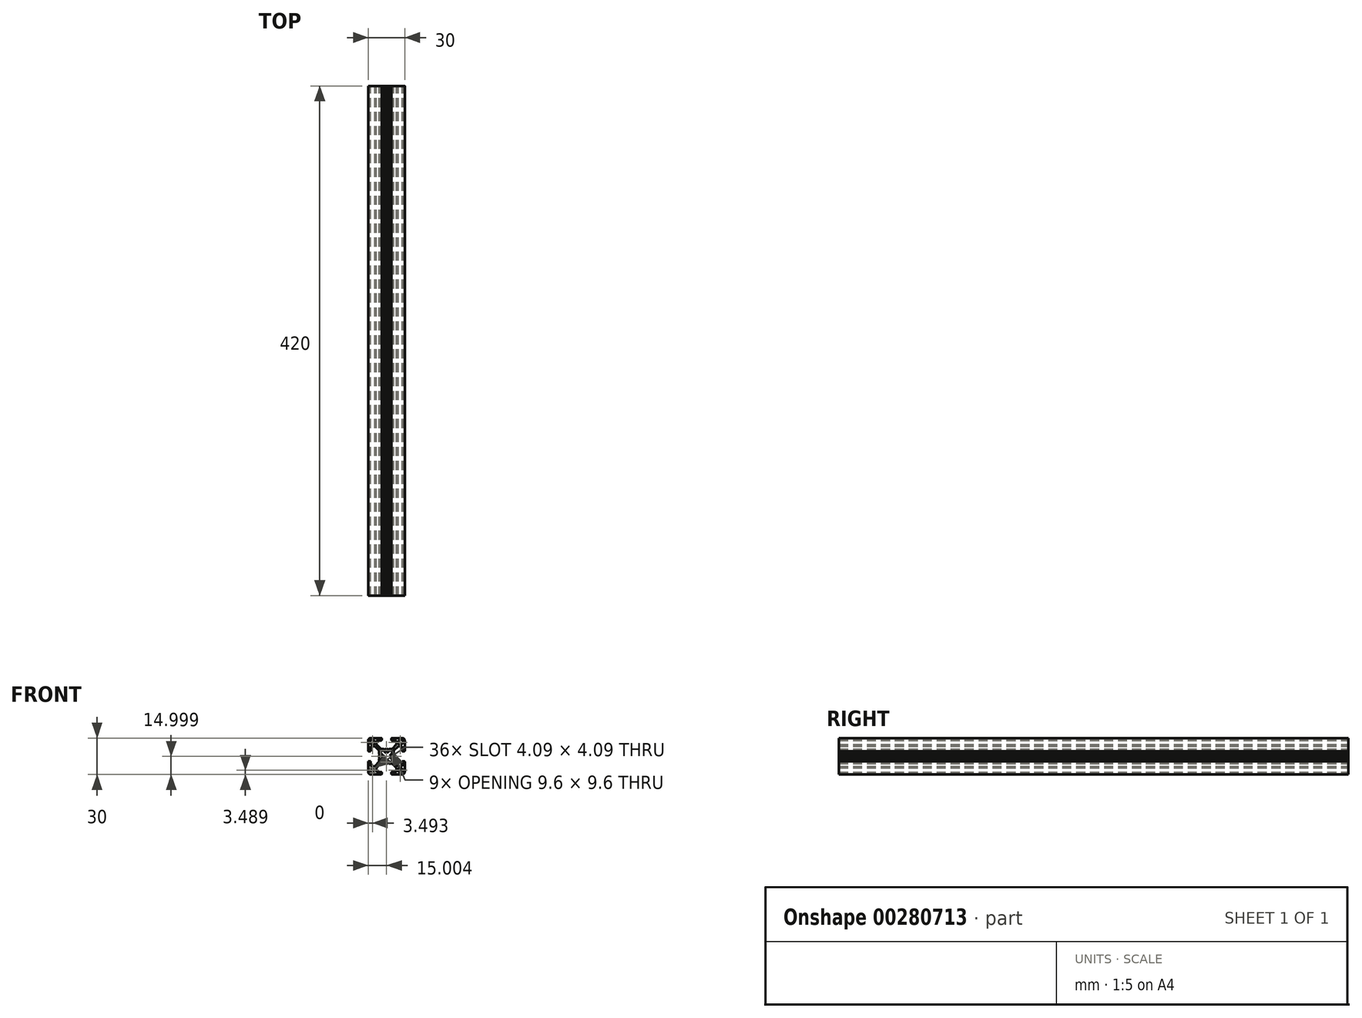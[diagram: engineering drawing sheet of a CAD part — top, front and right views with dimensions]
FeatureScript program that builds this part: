
annotation { "Feature Type Name" : "Feature", "Feature Type Description" : "" }
export const myFeature = defineFeature(function(context is Context, id is Id, definition is map)
    precondition{}
    {
        {
            var Q0;
            Q0=qCreatedBy(makeId("Front.planeOp"),FACE);
            var sketch = newSketch(context, id + "F0", { "sketchPlane" : qUnion([Q0])});
            skArc(sketch, "E0", {"start": v(22.08, 23.36) * mm, "mid": v(21.8, 23.24) * mm, "end": v(21.68, 22.96) * mm});
            skArc(sketch, "E1", {"start": v(21.68, 14.16) * mm, "mid": v(21.8, 13.88) * mm, "end": v(22.08, 13.76) * mm});
            skArc(sketch, "E2", {"start": v(11.48, 5.56) * mm, "mid": v(12.07, 4.15) * mm, "end": v(13.48, 3.56) * mm});
            skLineSegment(sketch, "E3", {"start": v(11.48, 14.16) * mm, "end": v(11.48, 5.56) * mm});
            skLineSegment(sketch, "E4", {"start": v(18.23, 5.56) * mm, "end": v(18.23, 8.9) * mm});
            skLineSegment(sketch, "E5", {"start": v(22.08, 3.56) * mm, "end": v(13.48, 3.56) * mm});
            skLineSegment(sketch, "E6", {"start": v(22.08, 5.56) * mm, "end": v(18.23, 5.56) * mm});
            skLineSegment(sketch, "E7", {"start": v(22.48, 5.16) * mm, "end": v(22.48, 3.96) * mm});
            skLineSegment(sketch, "E8", {"start": v(13.48, 10.3) * mm, "end": v(16.82, 10.3) * mm});
            skLineSegment(sketch, "E9", {"start": v(20.48, 13.97) * mm, "end": v(16.82, 10.3) * mm});
            skLineSegment(sketch, "E10", {"start": v(21.9, 12.56) * mm, "end": v(18.23, 8.9) * mm});
            skLineSegment(sketch, "E11", {"start": v(13.48, 14.16) * mm, "end": v(13.48, 10.3) * mm});
            skLineSegment(sketch, "E12", {"start": v(11.88, 14.56) * mm, "end": v(13.08, 14.56) * mm});
            skArc(sketch, "E13", {"start": v(22.08, 3.56) * mm, "mid": v(22.37, 3.68) * mm, "end": v(22.48, 3.96) * mm});
            skArc(sketch, "E14", {"start": v(22.48, 5.16) * mm, "mid": v(22.37, 5.44) * mm, "end": v(22.08, 5.56) * mm});
            skArc(sketch, "E15", {"start": v(13.48, 14.16) * mm, "mid": v(13.37, 14.44) * mm, "end": v(13.08, 14.56) * mm});
            skArc(sketch, "E16", {"start": v(11.88, 14.56) * mm, "mid": v(11.6, 14.44) * mm, "end": v(11.48, 14.16) * mm});
            skLineSegment(sketch, "E17", {"start": v(20.78, 18.56) * mm, "end": v(20.55, 18.16) * mm});
            skLineSegment(sketch, "E18", {"start": v(20.48, 13.97) * mm, "end": v(20.48, 16.06) * mm});
            skLineSegment(sketch, "E19", {"start": v(20.55, 17.66) * mm, "end": v(20.73, 17.34) * mm});
            skLineSegment(sketch, "E20", {"start": v(20.73, 17.34) * mm, "end": v(20.48, 16.06) * mm});
            skArc(sketch, "E21", {"start": v(20.55, 18.16) * mm, "mid": v(20.48, 17.9) * mm, "end": v(20.55, 17.66) * mm});
            skLineSegment(sketch, "E22", {"start": v(26.08, 12.63) * mm, "end": v(26.48, 12.86) * mm});
            skLineSegment(sketch, "E23", {"start": v(21.9, 12.56) * mm, "end": v(23.98, 12.56) * mm});
            skLineSegment(sketch, "E24", {"start": v(23.98, 12.56) * mm, "end": v(25.26, 12.8) * mm});
            skArc(sketch, "E25", {"start": v(25.58, 12.63) * mm, "mid": v(25.83, 12.56) * mm, "end": v(26.08, 12.63) * mm});
            skLineSegment(sketch, "E26", {"start": v(25.26, 12.8) * mm, "end": v(25.58, 12.63) * mm});
            skArc(sketch, "E27", {"start": v(25.5, 15.3) * mm, "mid": v(26.48, 15.16) * mm, "end": v(27.47, 15.3) * mm});
            skLineSegment(sketch, "E28", {"start": v(21.68, 14.16) * mm, "end": v(21.68, 15.9) * mm});
            skLineSegment(sketch, "E29", {"start": v(22.08, 13.76) * mm, "end": v(23.83, 13.76) * mm});
            skLineSegment(sketch, "E30", {"start": v(24.98, 14.3) * mm, "end": v(24.98, 14.92) * mm});
            skArc(sketch, "E31", {"start": v(25.5, 15.3) * mm, "mid": v(25.15, 15.24) * mm, "end": v(24.98, 14.92) * mm});
            skLineSegment(sketch, "E32", {"start": v(23.9, 13.77) * mm, "end": v(24.66, 13.91) * mm});
            skArc(sketch, "E33", {"start": v(24.66, 13.91) * mm, "mid": v(24.9, 14.05) * mm, "end": v(24.98, 14.3) * mm});
            skArc(sketch, "E34", {"start": v(23.83, 13.76) * mm, "mid": v(23.87, 13.76) * mm, "end": v(23.9, 13.77) * mm});
            skLineSegment(sketch, "E35", {"start": v(22.23, 17.06) * mm, "end": v(22.85, 17.06) * mm});
            skArc(sketch, "E36", {"start": v(22.85, 17.06) * mm, "mid": v(23.17, 17.22) * mm, "end": v(23.23, 17.58) * mm});
            skLineSegment(sketch, "E37", {"start": v(21.7, 15.98) * mm, "end": v(21.84, 16.74) * mm});
            skArc(sketch, "E38", {"start": v(22.23, 17.06) * mm, "mid": v(21.98, 16.97) * mm, "end": v(21.84, 16.74) * mm});
            skArc(sketch, "E39", {"start": v(21.7, 15.98) * mm, "mid": v(21.69, 15.94) * mm, "end": v(21.68, 15.9) * mm});
            skArc(sketch, "E40", {"start": v(30.88, 13.76) * mm, "mid": v(31.17, 13.88) * mm, "end": v(31.28, 14.16) * mm});
            skArc(sketch, "E41", {"start": v(39.48, 3.56) * mm, "mid": v(40.9, 4.15) * mm, "end": v(41.48, 5.56) * mm});
            skLineSegment(sketch, "E42", {"start": v(30.88, 3.56) * mm, "end": v(39.48, 3.56) * mm});
            skLineSegment(sketch, "E43", {"start": v(39.48, 10.3) * mm, "end": v(36.15, 10.3) * mm});
            skLineSegment(sketch, "E44", {"start": v(41.48, 14.16) * mm, "end": v(41.48, 5.56) * mm});
            skLineSegment(sketch, "E45", {"start": v(39.48, 14.16) * mm, "end": v(39.48, 10.3) * mm});
            skLineSegment(sketch, "E46", {"start": v(39.88, 14.56) * mm, "end": v(41.08, 14.56) * mm});
            skLineSegment(sketch, "E47", {"start": v(34.73, 5.56) * mm, "end": v(34.73, 8.9) * mm});
            skLineSegment(sketch, "E48", {"start": v(31.07, 12.56) * mm, "end": v(34.73, 8.9) * mm});
            skLineSegment(sketch, "E49", {"start": v(32.48, 13.97) * mm, "end": v(36.15, 10.3) * mm});
            skLineSegment(sketch, "E50", {"start": v(30.88, 5.56) * mm, "end": v(34.73, 5.56) * mm});
            skLineSegment(sketch, "E51", {"start": v(30.48, 3.96) * mm, "end": v(30.48, 5.16) * mm});
            skArc(sketch, "E52", {"start": v(41.48, 14.16) * mm, "mid": v(41.37, 14.44) * mm, "end": v(41.08, 14.56) * mm});
            skArc(sketch, "E53", {"start": v(39.88, 14.56) * mm, "mid": v(39.6, 14.44) * mm, "end": v(39.48, 14.16) * mm});
            skArc(sketch, "E54", {"start": v(30.88, 5.56) * mm, "mid": v(30.6, 5.44) * mm, "end": v(30.48, 5.16) * mm});
            skArc(sketch, "E55", {"start": v(30.48, 3.96) * mm, "mid": v(30.6, 3.68) * mm, "end": v(30.88, 3.56) * mm});
            skLineSegment(sketch, "E56", {"start": v(26.48, 12.86) * mm, "end": v(26.89, 12.63) * mm});
            skLineSegment(sketch, "E57", {"start": v(31.07, 12.56) * mm, "end": v(28.98, 12.56) * mm});
            skLineSegment(sketch, "E58", {"start": v(27.39, 12.63) * mm, "end": v(27.7, 12.8) * mm});
            skLineSegment(sketch, "E59", {"start": v(27.7, 12.8) * mm, "end": v(28.98, 12.56) * mm});
            skArc(sketch, "E60", {"start": v(26.89, 12.63) * mm, "mid": v(27.14, 12.56) * mm, "end": v(27.39, 12.63) * mm});
            skLineSegment(sketch, "E61", {"start": v(32.42, 18.16) * mm, "end": v(32.18, 18.56) * mm});
            skLineSegment(sketch, "E62", {"start": v(32.48, 13.97) * mm, "end": v(32.48, 16.06) * mm});
            skLineSegment(sketch, "E63", {"start": v(32.48, 16.06) * mm, "end": v(32.23, 17.34) * mm});
            skArc(sketch, "E64", {"start": v(32.42, 17.66) * mm, "mid": v(32.48, 17.9) * mm, "end": v(32.42, 18.16) * mm});
            skLineSegment(sketch, "E65", {"start": v(32.23, 17.34) * mm, "end": v(32.42, 17.66) * mm});
            skArc(sketch, "E66", {"start": v(29.74, 17.58) * mm, "mid": v(29.88, 18.56) * mm, "end": v(29.74, 19.54) * mm});
            skLineSegment(sketch, "E67", {"start": v(30.88, 13.76) * mm, "end": v(29.14, 13.76) * mm});
            skLineSegment(sketch, "E68", {"start": v(31.28, 14.16) * mm, "end": v(31.28, 15.9) * mm});
            skLineSegment(sketch, "E69", {"start": v(30.74, 17.06) * mm, "end": v(30.12, 17.06) * mm});
            skArc(sketch, "E70", {"start": v(29.74, 17.58) * mm, "mid": v(29.8, 17.22) * mm, "end": v(30.12, 17.06) * mm});
            skLineSegment(sketch, "E71", {"start": v(31.28, 15.98) * mm, "end": v(31.13, 16.74) * mm});
            skArc(sketch, "E72", {"start": v(31.13, 16.74) * mm, "mid": v(31, 16.97) * mm, "end": v(30.74, 17.06) * mm});
            skArc(sketch, "E73", {"start": v(31.28, 15.9) * mm, "mid": v(31.28, 15.94) * mm, "end": v(31.28, 15.98) * mm});
            skLineSegment(sketch, "E74", {"start": v(27.98, 14.3) * mm, "end": v(27.98, 14.92) * mm});
            skArc(sketch, "E75", {"start": v(27.98, 14.92) * mm, "mid": v(27.82, 15.24) * mm, "end": v(27.47, 15.3) * mm});
            skLineSegment(sketch, "E76", {"start": v(29.06, 13.77) * mm, "end": v(28.3, 13.91) * mm});
            skArc(sketch, "E77", {"start": v(27.98, 14.3) * mm, "mid": v(28.08, 14.05) * mm, "end": v(28.3, 13.91) * mm});
            skArc(sketch, "E78", {"start": v(29.06, 13.77) * mm, "mid": v(29.1, 13.76) * mm, "end": v(29.14, 13.76) * mm});
            skArc(sketch, "E79", {"start": v(31.28, 22.96) * mm, "mid": v(31.17, 23.24) * mm, "end": v(30.88, 23.36) * mm});
            skArc(sketch, "E80", {"start": v(41.48, 31.56) * mm, "mid": v(40.9, 32.97) * mm, "end": v(39.48, 33.56) * mm});
            skLineSegment(sketch, "E81", {"start": v(41.48, 22.96) * mm, "end": v(41.48, 31.56) * mm});
            skLineSegment(sketch, "E82", {"start": v(34.73, 31.56) * mm, "end": v(34.73, 28.22) * mm});
            skLineSegment(sketch, "E83", {"start": v(30.88, 33.56) * mm, "end": v(39.48, 33.56) * mm});
            skLineSegment(sketch, "E84", {"start": v(30.88, 31.56) * mm, "end": v(34.73, 31.56) * mm});
            skLineSegment(sketch, "E85", {"start": v(30.48, 31.96) * mm, "end": v(30.48, 33.16) * mm});
            skLineSegment(sketch, "E86", {"start": v(39.48, 26.8) * mm, "end": v(36.15, 26.8) * mm});
            skLineSegment(sketch, "E87", {"start": v(32.48, 23.15) * mm, "end": v(36.15, 26.8) * mm});
            skLineSegment(sketch, "E88", {"start": v(31.07, 24.56) * mm, "end": v(34.73, 28.22) * mm});
            skLineSegment(sketch, "E89", {"start": v(39.48, 22.96) * mm, "end": v(39.48, 26.8) * mm});
            skLineSegment(sketch, "E90", {"start": v(41.08, 22.56) * mm, "end": v(39.88, 22.56) * mm});
            skArc(sketch, "E91", {"start": v(30.88, 33.56) * mm, "mid": v(30.6, 33.44) * mm, "end": v(30.48, 33.16) * mm});
            skArc(sketch, "E92", {"start": v(30.48, 31.96) * mm, "mid": v(30.6, 31.68) * mm, "end": v(30.88, 31.56) * mm});
            skArc(sketch, "E93", {"start": v(39.48, 22.96) * mm, "mid": v(39.6, 22.68) * mm, "end": v(39.88, 22.56) * mm});
            skArc(sketch, "E94", {"start": v(41.08, 22.56) * mm, "mid": v(41.37, 22.68) * mm, "end": v(41.48, 22.96) * mm});
            skLineSegment(sketch, "E95", {"start": v(32.18, 18.56) * mm, "end": v(32.42, 18.96) * mm});
            skLineSegment(sketch, "E96", {"start": v(32.48, 23.15) * mm, "end": v(32.48, 21.06) * mm});
            skLineSegment(sketch, "E97", {"start": v(32.42, 19.46) * mm, "end": v(32.23, 19.78) * mm});
            skLineSegment(sketch, "E98", {"start": v(32.23, 19.78) * mm, "end": v(32.48, 21.06) * mm});
            skArc(sketch, "E99", {"start": v(32.42, 18.96) * mm, "mid": v(32.48, 19.21) * mm, "end": v(32.42, 19.46) * mm});
            skLineSegment(sketch, "E100", {"start": v(26.89, 24.5) * mm, "end": v(26.48, 24.26) * mm});
            skLineSegment(sketch, "E101", {"start": v(31.07, 24.56) * mm, "end": v(28.98, 24.56) * mm});
            skLineSegment(sketch, "E102", {"start": v(28.98, 24.56) * mm, "end": v(27.7, 24.31) * mm});
            skArc(sketch, "E103", {"start": v(27.39, 24.5) * mm, "mid": v(27.14, 24.56) * mm, "end": v(26.89, 24.5) * mm});
            skLineSegment(sketch, "E104", {"start": v(27.7, 24.31) * mm, "end": v(27.39, 24.5) * mm});
            skArc(sketch, "E105", {"start": v(27.47, 21.81) * mm, "mid": v(26.48, 21.96) * mm, "end": v(25.5, 21.81) * mm});
            skLineSegment(sketch, "E106", {"start": v(31.28, 22.96) * mm, "end": v(31.28, 21.21) * mm});
            skLineSegment(sketch, "E107", {"start": v(30.88, 23.36) * mm, "end": v(29.14, 23.36) * mm});
            skLineSegment(sketch, "E108", {"start": v(27.98, 22.81) * mm, "end": v(27.98, 22.2) * mm});
            skArc(sketch, "E109", {"start": v(27.47, 21.81) * mm, "mid": v(27.82, 21.88) * mm, "end": v(27.98, 22.2) * mm});
            skLineSegment(sketch, "E110", {"start": v(29.06, 23.35) * mm, "end": v(28.3, 23.2) * mm});
            skArc(sketch, "E111", {"start": v(28.3, 23.2) * mm, "mid": v(28.08, 23.07) * mm, "end": v(27.98, 22.81) * mm});
            skArc(sketch, "E112", {"start": v(29.14, 23.36) * mm, "mid": v(29.1, 23.36) * mm, "end": v(29.06, 23.35) * mm});
            skLineSegment(sketch, "E113", {"start": v(30.74, 20.06) * mm, "end": v(30.12, 20.06) * mm});
            skArc(sketch, "E114", {"start": v(30.12, 20.06) * mm, "mid": v(29.8, 19.9) * mm, "end": v(29.74, 19.54) * mm});
            skLineSegment(sketch, "E115", {"start": v(31.28, 21.14) * mm, "end": v(31.13, 20.38) * mm});
            skArc(sketch, "E116", {"start": v(30.74, 20.06) * mm, "mid": v(31, 20.15) * mm, "end": v(31.13, 20.38) * mm});
            skArc(sketch, "E117", {"start": v(31.28, 21.14) * mm, "mid": v(31.28, 21.18) * mm, "end": v(31.28, 21.21) * mm});
            skArc(sketch, "E118", {"start": v(13.48, 33.56) * mm, "mid": v(12.07, 32.97) * mm, "end": v(11.48, 31.56) * mm});
            skLineSegment(sketch, "E119", {"start": v(22.08, 33.56) * mm, "end": v(13.48, 33.56) * mm});
            skLineSegment(sketch, "E120", {"start": v(13.48, 26.8) * mm, "end": v(16.82, 26.8) * mm});
            skLineSegment(sketch, "E121", {"start": v(11.48, 22.96) * mm, "end": v(11.48, 31.56) * mm});
            skLineSegment(sketch, "E122", {"start": v(13.48, 22.96) * mm, "end": v(13.48, 26.8) * mm});
            skLineSegment(sketch, "E123", {"start": v(13.08, 22.56) * mm, "end": v(11.88, 22.56) * mm});
            skLineSegment(sketch, "E124", {"start": v(18.23, 31.56) * mm, "end": v(18.23, 28.22) * mm});
            skLineSegment(sketch, "E125", {"start": v(21.9, 24.56) * mm, "end": v(18.23, 28.22) * mm});
            skLineSegment(sketch, "E126", {"start": v(20.48, 23.15) * mm, "end": v(16.82, 26.8) * mm});
            skLineSegment(sketch, "E127", {"start": v(22.08, 31.56) * mm, "end": v(18.23, 31.56) * mm});
            skLineSegment(sketch, "E128", {"start": v(22.48, 33.16) * mm, "end": v(22.48, 31.96) * mm});
            skArc(sketch, "E129", {"start": v(11.48, 22.96) * mm, "mid": v(11.6, 22.68) * mm, "end": v(11.88, 22.56) * mm});
            skArc(sketch, "E130", {"start": v(13.08, 22.56) * mm, "mid": v(13.37, 22.68) * mm, "end": v(13.48, 22.96) * mm});
            skArc(sketch, "E131", {"start": v(22.08, 31.56) * mm, "mid": v(22.37, 31.68) * mm, "end": v(22.48, 31.96) * mm});
            skArc(sketch, "E132", {"start": v(22.48, 33.16) * mm, "mid": v(22.37, 33.44) * mm, "end": v(22.08, 33.56) * mm});
            skLineSegment(sketch, "E133", {"start": v(26.48, 24.26) * mm, "end": v(26.08, 24.5) * mm});
            skLineSegment(sketch, "E134", {"start": v(21.9, 24.56) * mm, "end": v(23.98, 24.56) * mm});
            skLineSegment(sketch, "E135", {"start": v(25.58, 24.5) * mm, "end": v(25.26, 24.31) * mm});
            skLineSegment(sketch, "E136", {"start": v(25.26, 24.31) * mm, "end": v(23.98, 24.56) * mm});
            skArc(sketch, "E137", {"start": v(26.08, 24.5) * mm, "mid": v(25.83, 24.56) * mm, "end": v(25.58, 24.5) * mm});
            skLineSegment(sketch, "E138", {"start": v(20.55, 18.96) * mm, "end": v(20.78, 18.56) * mm});
            skLineSegment(sketch, "E139", {"start": v(20.48, 23.15) * mm, "end": v(20.48, 21.06) * mm});
            skLineSegment(sketch, "E140", {"start": v(20.48, 21.06) * mm, "end": v(20.73, 19.78) * mm});
            skArc(sketch, "E141", {"start": v(20.55, 19.46) * mm, "mid": v(20.48, 19.21) * mm, "end": v(20.55, 18.96) * mm});
            skLineSegment(sketch, "E142", {"start": v(20.73, 19.78) * mm, "end": v(20.55, 19.46) * mm});
            skArc(sketch, "E143", {"start": v(23.23, 19.54) * mm, "mid": v(23.08, 18.56) * mm, "end": v(23.23, 17.58) * mm});
            skLineSegment(sketch, "E144", {"start": v(22.08, 23.36) * mm, "end": v(23.83, 23.36) * mm});
            skLineSegment(sketch, "E145", {"start": v(21.68, 22.96) * mm, "end": v(21.68, 21.21) * mm});
            skLineSegment(sketch, "E146", {"start": v(22.23, 20.06) * mm, "end": v(22.85, 20.06) * mm});
            skArc(sketch, "E147", {"start": v(23.23, 19.54) * mm, "mid": v(23.17, 19.9) * mm, "end": v(22.85, 20.06) * mm});
            skLineSegment(sketch, "E148", {"start": v(21.7, 21.14) * mm, "end": v(21.84, 20.38) * mm});
            skArc(sketch, "E149", {"start": v(21.84, 20.38) * mm, "mid": v(21.98, 20.15) * mm, "end": v(22.23, 20.06) * mm});
            skArc(sketch, "E150", {"start": v(21.68, 21.21) * mm, "mid": v(21.69, 21.18) * mm, "end": v(21.7, 21.14) * mm});
            skLineSegment(sketch, "E151", {"start": v(24.98, 22.81) * mm, "end": v(24.98, 22.2) * mm});
            skArc(sketch, "E152", {"start": v(24.98, 22.2) * mm, "mid": v(25.15, 21.88) * mm, "end": v(25.5, 21.81) * mm});
            skLineSegment(sketch, "E153", {"start": v(23.9, 23.35) * mm, "end": v(24.66, 23.2) * mm});
            skArc(sketch, "E154", {"start": v(24.98, 22.81) * mm, "mid": v(24.9, 23.07) * mm, "end": v(24.66, 23.2) * mm});
            skArc(sketch, "E155", {"start": v(23.9, 23.35) * mm, "mid": v(23.87, 23.36) * mm, "end": v(23.83, 23.36) * mm});
            skArc(sketch, "E156", {"start": v(14.13, 8.64) * mm, "mid": v(13.44, 5.52) * mm, "end": v(16.57, 6.2) * mm});
            skLineSegment(sketch, "E157", {"start": v(16.94, 7.22) * mm, "end": v(16.57, 6.2) * mm});
            skLineSegment(sketch, "E158", {"start": v(15.14, 9.01) * mm, "end": v(14.13, 8.64) * mm});
            skArc(sketch, "E159", {"start": v(16.94, 7.22) * mm, "mid": v(16.61, 8.69) * mm, "end": v(15.14, 9.01) * mm});
            skArc(sketch, "E160", {"start": v(16.57, 30.9) * mm, "mid": v(13.44, 31.6) * mm, "end": v(14.13, 28.47) * mm});
            skLineSegment(sketch, "E161", {"start": v(16.94, 29.9) * mm, "end": v(16.57, 30.9) * mm});
            skLineSegment(sketch, "E162", {"start": v(15.14, 28.1) * mm, "end": v(14.13, 28.47) * mm});
            skArc(sketch, "E163", {"start": v(15.14, 28.1) * mm, "mid": v(16.61, 28.43) * mm, "end": v(16.94, 29.9) * mm});
            skArc(sketch, "E164", {"start": v(36.4, 6.2) * mm, "mid": v(39.53, 5.52) * mm, "end": v(38.83, 8.64) * mm});
            skLineSegment(sketch, "E165", {"start": v(36.03, 7.22) * mm, "end": v(36.4, 6.2) * mm});
            skLineSegment(sketch, "E166", {"start": v(37.83, 9.01) * mm, "end": v(38.83, 8.64) * mm});
            skArc(sketch, "E167", {"start": v(37.83, 9.01) * mm, "mid": v(36.36, 8.69) * mm, "end": v(36.03, 7.22) * mm});
            skArc(sketch, "E168", {"start": v(38.83, 28.47) * mm, "mid": v(39.53, 31.6) * mm, "end": v(36.4, 30.9) * mm});
            skLineSegment(sketch, "E169", {"start": v(36.03, 29.9) * mm, "end": v(36.4, 30.9) * mm});
            skLineSegment(sketch, "E170", {"start": v(37.83, 28.1) * mm, "end": v(38.83, 28.47) * mm});
            skArc(sketch, "E171", {"start": v(36.03, 29.9) * mm, "mid": v(36.36, 28.43) * mm, "end": v(37.83, 28.1) * mm});
            skLineSegment(sketch, "E172", {"start": v(26.48, 0.56) * mm, "end": v(26.48, 36.56) * mm});
            skLineSegment(sketch, "E173", {"start": v(44.48, 18.56) * mm, "end": v(8.48, 18.56) * mm});
            skSolve(sketch);
        }
        {
            var Q0;
            Q0 = qSketchRegion(id + "F0", true);
            extrude(context, id + "F1", {"entities" : qUnion([Q0]), "depth" : 420 * mm});
        }
    });
